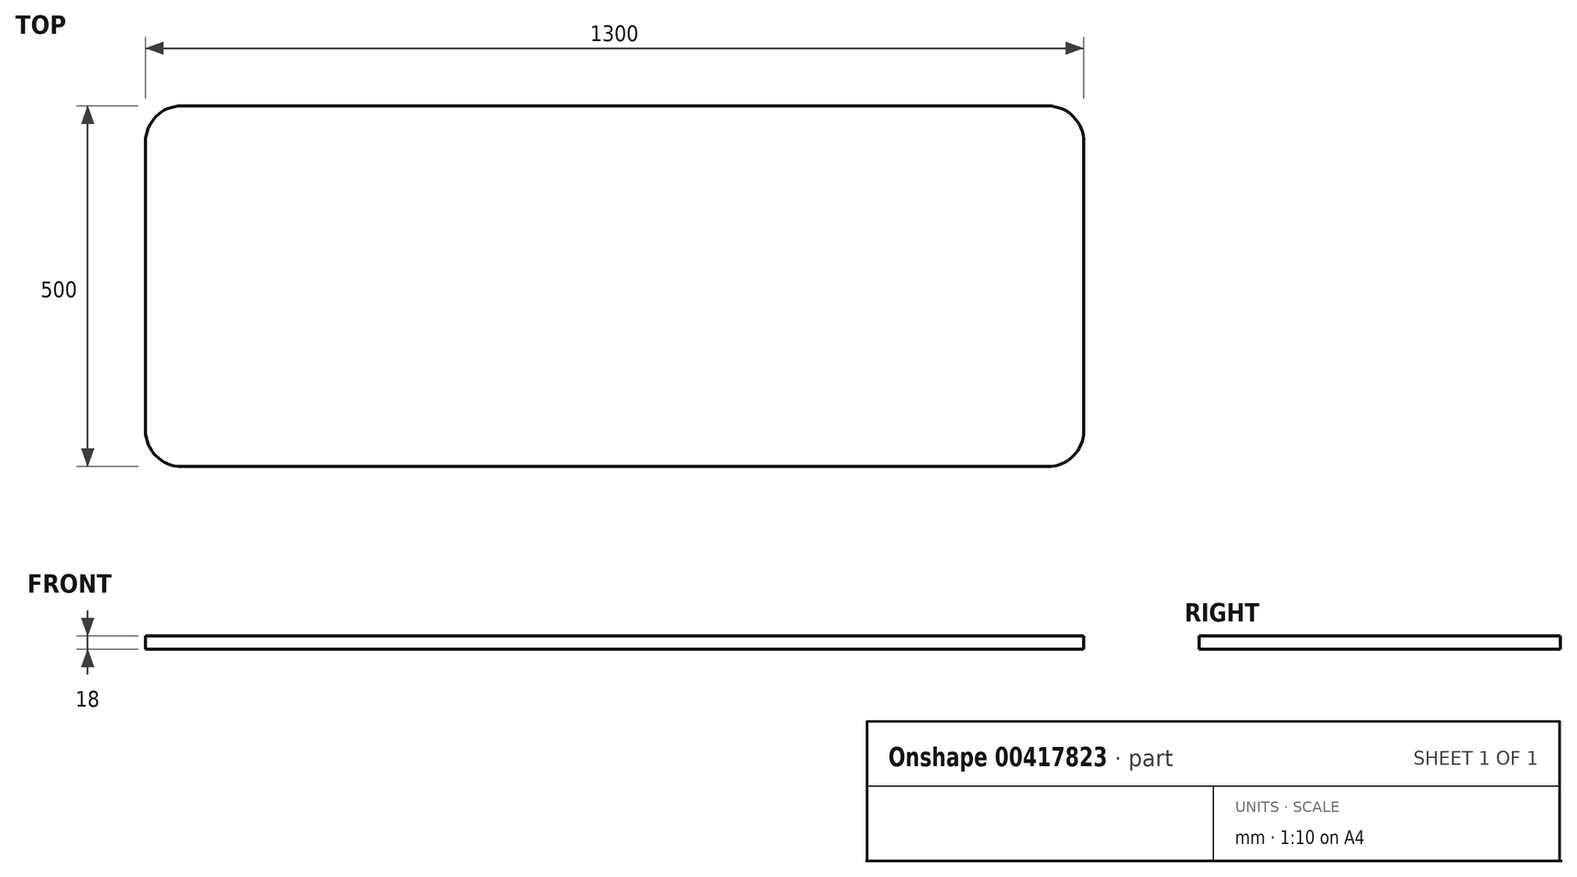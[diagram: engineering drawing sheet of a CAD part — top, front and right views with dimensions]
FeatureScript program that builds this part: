
annotation { "Feature Type Name" : "Feature", "Feature Type Description" : "" }
export const myFeature = defineFeature(function(context is Context, id is Id, definition is map)
    precondition{}
    {
        {
            var Q0;
            Q0=qCreatedBy(makeId("Top.planeOp"),FACE);
            var sketch = newSketch(context, id + "F0", { "sketchPlane" : qUnion([Q0])});
            skLineSegment(sketch, "E0.bottom", {"start": v(600, 200) * mm, "end": v(-600, 200) * mm, "construction": true});
            skLineSegment(sketch, "E0.top", {"start": v(600, -200) * mm, "end": v(-600, -200) * mm, "construction": true});
            skLineSegment(sketch, "E0.left", {"start": v(600, 200) * mm, "end": v(600, -200) * mm, "construction": true});
            skLineSegment(sketch, "E0.right", {"start": v(-600, 200) * mm, "end": v(-600, -200) * mm, "construction": true});
            skPoint(sketch, "E0.middle", {"position": v(0, 0) * mm});
            skLineSegment(sketch, "E1.0", {"start": v(600, 250) * mm, "end": v(-600, 250) * mm});
            skLineSegment(sketch, "E1.1", {"start": v(650, 200) * mm, "end": v(650, -200) * mm});
            skLineSegment(sketch, "E1.2", {"start": v(600, -250) * mm, "end": v(-600, -250) * mm});
            skLineSegment(sketch, "E1.3", {"start": v(-650, 200) * mm, "end": v(-650, -200) * mm});
            skPoint(sketch, "E2.visualSharp", {"position": v(-650, 250) * mm});
            skArc(sketch, "E2.filletArc", {"start": v(-600, 250) * mm, "mid": v(-635.36, 235.36) * mm, "end": v(-650, 200) * mm});
            skPoint(sketch, "E3.visualSharp", {"position": v(-650, -250) * mm});
            skArc(sketch, "E3.filletArc", {"start": v(-650, -200) * mm, "mid": v(-635.36, -235.36) * mm, "end": v(-600, -250) * mm});
            skPoint(sketch, "E4.visualSharp", {"position": v(650, -250) * mm});
            skArc(sketch, "E4.filletArc", {"start": v(600, -250) * mm, "mid": v(635.36, -235.36) * mm, "end": v(650, -200) * mm});
            skPoint(sketch, "E5.visualSharp", {"position": v(650, 250) * mm});
            skArc(sketch, "E5.filletArc", {"start": v(650, 200) * mm, "mid": v(635.36, 235.36) * mm, "end": v(600, 250) * mm});
            skSolve(sketch);
        }
        {
            var Q0;
            Q0 = qSketchRegion(id + "F0", true);
            extrude(context, id + "F1", {"entities" : qUnion([Q0]), "depth" : 18 * mm});
        }
    });
